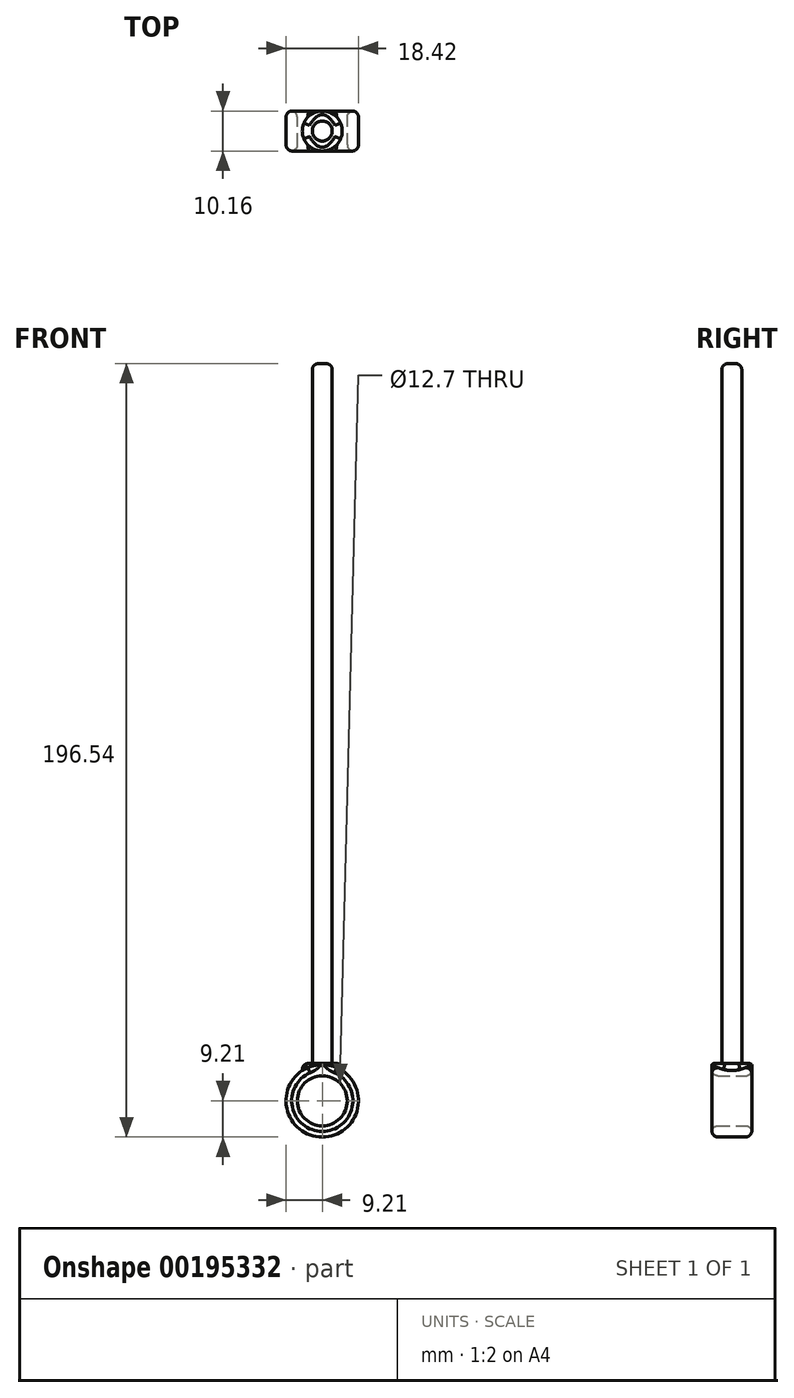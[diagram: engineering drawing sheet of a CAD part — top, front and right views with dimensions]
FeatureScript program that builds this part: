
annotation { "Feature Type Name" : "Feature", "Feature Type Description" : "" }
export const myFeature = defineFeature(function(context is Context, id is Id, definition is map)
    precondition{}
    {
        {
            var Q0;
            Q0=qCreatedBy(makeId("Top.planeOp"),FACE);
            var sketch = newSketch(context, id + "F0", { "sketchPlane" : qUnion([Q0])});
            skCircle(sketch, "E0", {"center": v(0, 0) * mm, "radius": 5.08 * mm});
            skSolve(sketch);
        }
        {
            var Q0;
            Q0 = qSketchRegion(id + "F0", true);
            extrude(context, id + "F1", {"entities" : qUnion([Q0]), "depth" : 3.17 * mm});
        }
        {
            var Q0;
            Q0=makeQuery(id+"F1.opExtrude","CAP_FACE",FACE,{"disambiguationData":[OSD([sQuery(id+"F0.wireOp",EDGE,"E0")])],"isStart":false});
            var sketch = newSketch(context, id + "F2", { "sketchPlane" : qUnion([Q0])});
            skCircle(sketch, "E1", {"center": v(0, 0) * mm, "radius": 2.54 * mm});
            skSolve(sketch);
        }
        {
            var Q0;
            Q0 = qSketchRegion(id + "F2", true);
            extrude(context, id + "F3", {"entities" : qUnion([Q0]), "operationType" : NewBodyOperationType.ADD, "depth" : 177.8 * mm});
        }
        {
            var Q0;
            Q0=makeQuery(id+"F3.opExtrude","CAP_EDGE",EDGE,{"disambiguationData":[OSD([sQuery(id+"F2.wireOp",EDGE,"E1")])],"isStart":false});
            fillet(context, id + "F4", {"entities" : qUnion([Q0]), "radius" : 1.59 * mm, "tangentPropagation" : true, "allowEdgeOverflow" : false});
        }
        {
            var Q0;
            Q0=qCreatedBy(makeId("Front.planeOp"),FACE);
            var sketch = newSketch(context, id + "F5", { "sketchPlane" : qUnion([Q0])});
            skCircle(sketch, "E2", {"center": v(0, -6.35) * mm, "radius": 9.2 * mm});
            skCircle(sketch, "E3", {"center": v(0, -6.35) * mm, "radius": 6.35 * mm});
            skSolve(sketch);
        }
        {
            var Q0;
            Q0 = qSketchRegion(id + "F5", true);
            extrude(context, id + "F6", {"entities" : qUnion([Q0]), "operationType" : NewBodyOperationType.ADD, "endBound" : BoundingType.SYMMETRIC, "depth" : 10.16 * mm});
        }
        {
            var Q0;
            Q0=makeQuery(id+"F6.opExtrude","CAP_EDGE",EDGE,{"disambiguationData":[OSD([sQuery(id+"F5.wireOp",EDGE,"E2")])],"isStart":false});
            var Q1;
            Q1=makeQuery(id+"F6.opExtrude","CAP_EDGE",EDGE,{"disambiguationData":[OSD([sQuery(id+"F5.wireOp",EDGE,"E3")])],"isStart":false});
            var Q2;
            Q2=makeQuery(id+"F6.opExtrude","CAP_EDGE",EDGE,{"disambiguationData":[OSD([sQuery(id+"F5.wireOp",EDGE,"E2")])],"isStart":true});
            var Q3;
            Q3=makeQuery(id+"F6.opExtrude","CAP_EDGE",EDGE,{"disambiguationData":[OSD([sQuery(id+"F5.wireOp",EDGE,"E3")])],"isStart":true});
            var Q4;
            Q4=makeQuery(id+"F1.opExtrude","CAP_EDGE",EDGE,{"disambiguationData":[OSD([sQuery(id+"F0.wireOp",EDGE,"E0")])],"isStart":false});
            fillet(context, id + "F7", {"entities" : qUnion([Q0, Q1, Q2, Q3, Q4]), "radius" : 1.59 * mm, "tangentPropagation" : true, "allowEdgeOverflow" : false});
        }
    });
